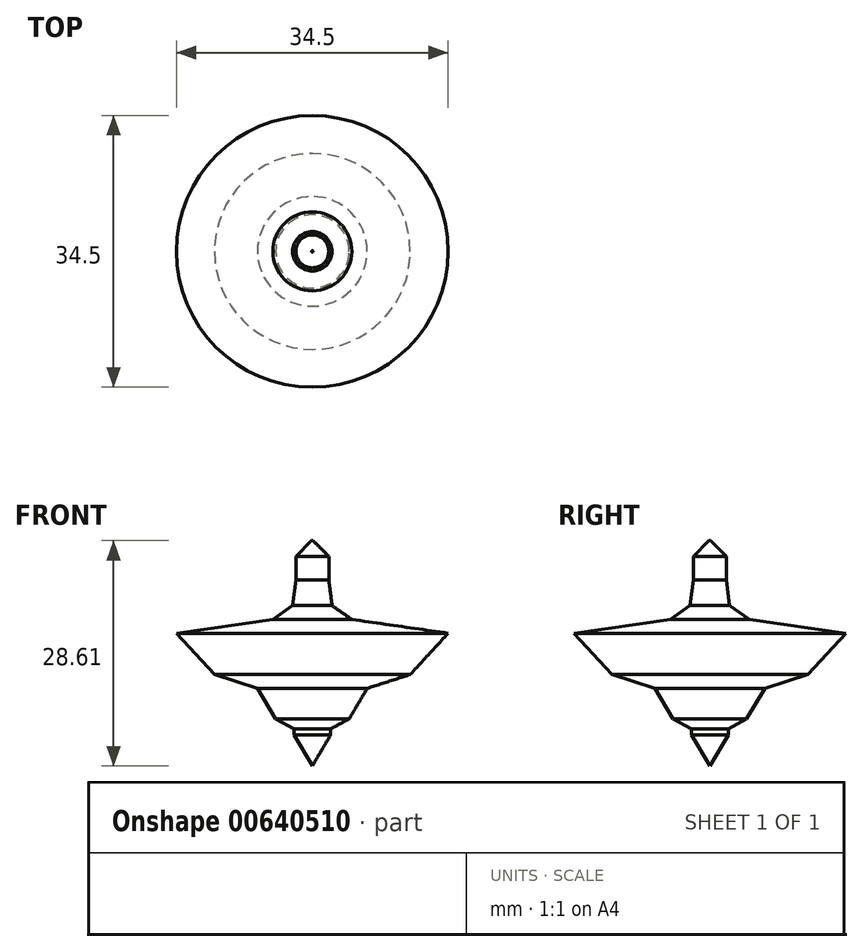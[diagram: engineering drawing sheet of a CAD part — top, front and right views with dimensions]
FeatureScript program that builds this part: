
annotation { "Feature Type Name" : "Feature", "Feature Type Description" : "" }
export const myFeature = defineFeature(function(context is Context, id is Id, definition is map)
    precondition{}
    {
        {
            var Q0;
            Q0=qCreatedBy(makeId("Front.planeOp"),FACE);
            var sketch = newSketch(context, id + "F0", { "sketchPlane" : qUnion([Q0])});
            skLineSegment(sketch, "E0", {"start": v(0, 0) * mm, "end": v(-6.97, 11.8) * mm});
            skLineSegment(sketch, "E1", {"start": v(-6.97, 11.8) * mm, "end": v(-12.44, 13.55) * mm});
            skLineSegment(sketch, "E2", {"start": v(-12.44, 13.55) * mm, "end": v(-17.25, 18.8) * mm});
            skLineSegment(sketch, "E3", {"start": v(-17.25, 18.8) * mm, "end": v(-5.01, 20.56) * mm});
            skLineSegment(sketch, "E4", {"start": v(-5.01, 20.56) * mm, "end": v(0, 20.56) * mm});
            skLineSegment(sketch, "E5", {"start": v(0, 20.56) * mm, "end": v(0, 0) * mm});
            skLineSegment(sketch, "E6", {"start": v(-3.48, 5.9) * mm, "end": v(0, 5.9) * mm});
            skLineSegment(sketch, "E7", {"start": v(-1.74, 7.9) * mm, "end": v(0, 7.9) * mm});
            skLineSegment(sketch, "E8", {"start": v(0, 7.9) * mm, "end": v(-4.66, 7.9) * mm});
            skLineSegment(sketch, "E9", {"start": v(0, 20.56) * mm, "end": v(0, 25.56) * mm});
            skLineSegment(sketch, "E10", {"start": v(0, 25.56) * mm, "end": v(-2.1, 25.56) * mm});
            skLineSegment(sketch, "E11", {"start": v(-2.1, 25.56) * mm, "end": v(-2.5, 22.31) * mm});
            skPoint(sketch, "E11.endSnap0", {"position": v(-2.5, 20.56) * mm});
            skLineSegment(sketch, "E12", {"start": v(-2.5, 22.31) * mm, "end": v(-5.01, 20.56) * mm});
            skLineSegment(sketch, "E13", {"start": v(-4.66, 7.9) * mm, "end": v(-2.33, 6.67) * mm});
            skPoint(sketch, "E13.endSnap0", {"position": v(-2.33, 7.9) * mm});
            skLineSegment(sketch, "E14", {"start": v(-2.33, 6.67) * mm, "end": v(-2.33, 5.9) * mm});
            skLineSegment(sketch, "E15", {"start": v(-2.33, 5.9) * mm, "end": v(0, 1.95) * mm});
            skSolve(sketch);
        }
        {
            var Q0;
            {var subQ0=sQuery(id+"F0.wireOp",EDGE,"E1");Q0=makeQuery(id+"F0.imprint","IMPRINT",FACE,{"disambiguationData":[TD([[makeQuery(id+"F0.imprint","IMPRINT",EDGE,{"derivedFrom":subQ0}),-1.0]])]});}
            var Q1;
            Q1=makeQuery(id+"F0.imprint","IMPRINT",FACE,{"disambiguationData":[TD([[makeQuery(id+"F0.imprint","IMPRINT",EDGE,{"derivedFrom":sQuery(id+"F0.wireOp",EDGE,"E4")}),1.0]])]});
            var Q2;
            {var subQ0=sQuery(id+"F0.wireOp",EDGE,"E13");Q2=makeQuery(id+"F0.imprint","IMPRINT",FACE,{"disambiguationData":[TD([[makeQuery(id+"F0.imprint","IMPRINT",EDGE,{"derivedFrom":subQ0}),1.0]])]});}
            var Q3;
            {var subQ3=sQuery(id+"F0.wireOp",EDGE,"E15");Q3=makeQuery(id+"F0.imprint","IMPRINT",FACE,{"disambiguationData":[TD([[makeQuery(id+"F0.imprint","IMPRINT",EDGE,{"derivedFrom":subQ3}),1.0]])]});}
            var Q4;
            Q4=sQuery(id+"F0.wireOp",EDGE,"E5");
            revolve(context, id + "F1", {"entities" : qUnion([Q0, Q1, Q2, Q3]), "axis" : qUnion([Q4]), "revolveType" : RevolveType.FULL});
        }
        {
            var Q0;
            Q0=makeQuery(id+"F1.opRevolve","SWEPT_FACE",FACE,{"disambiguationData":[OSD([sQuery(id+"F0.wireOp",EDGE,"E10")])]});
            extrude(context, id + "F2", {"entities" : qUnion([Q0]), "operationType" : NewBodyOperationType.ADD, "depth" : 5 * mm, "offsetDistance" : 25 * mm});
        }
        {
            var Q0;
            Q0=makeQuery(id+"F2.opExtrude","CAP_EDGE",EDGE,{"disambiguationData":[OSD([sQuery(id+"F0.wireOp",EDGE,"E10"),sQuery(id+"F0.wireOp",EDGE,"E11")])],"isStart":false});
            chamfer(context, id + "F3", {"entities" : qUnion([Q0]), "width" : 2 * mm, "tangentPropagation" : true});
        }
    });
